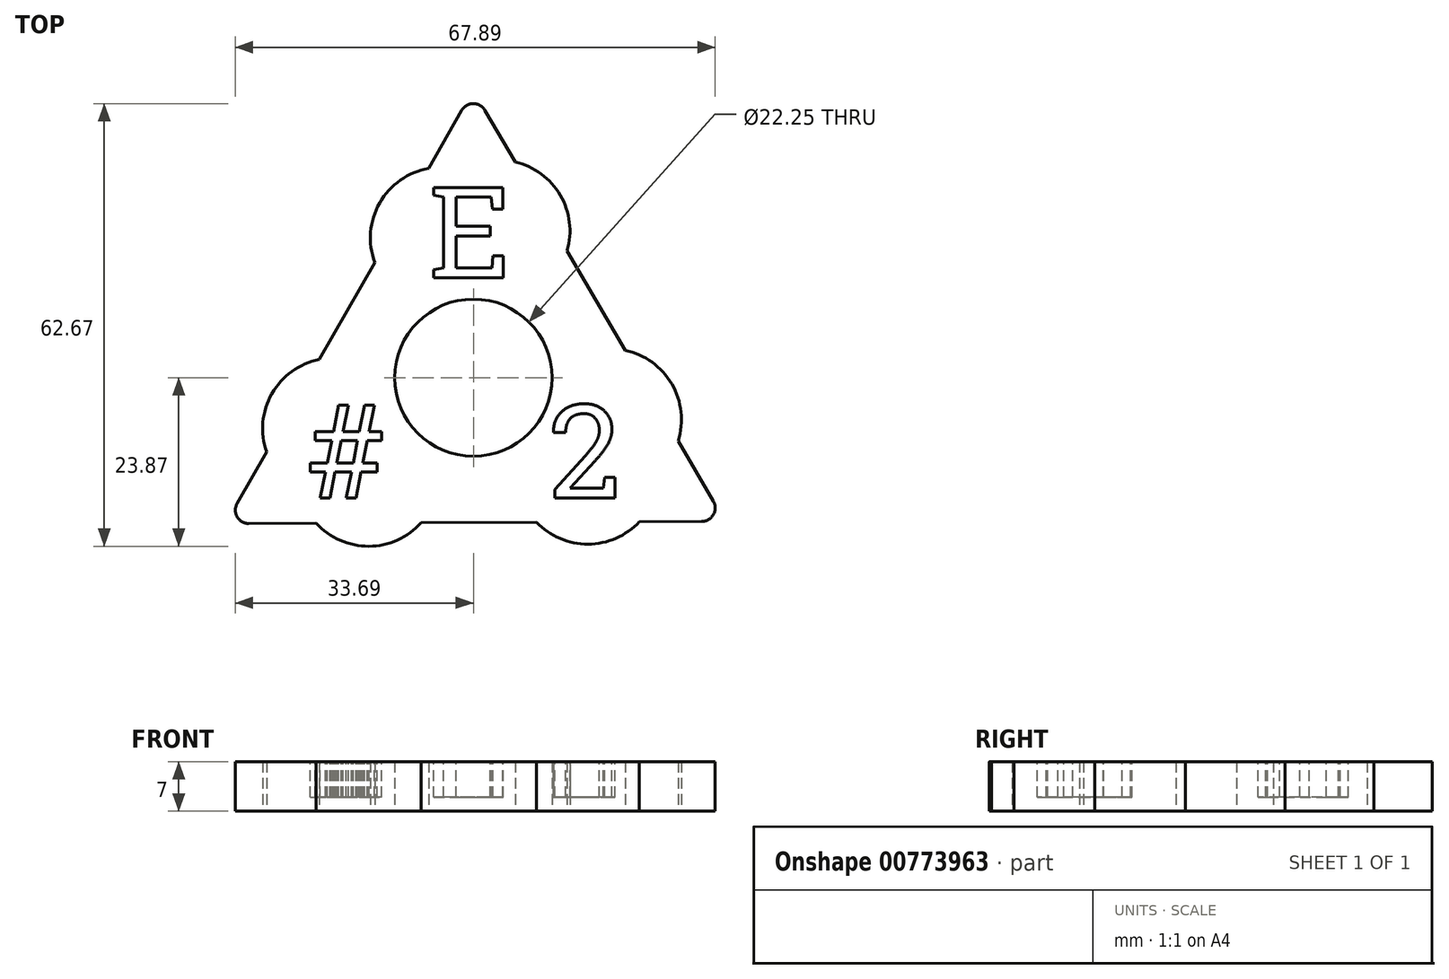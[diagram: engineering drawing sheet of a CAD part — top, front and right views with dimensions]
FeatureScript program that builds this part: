
annotation { "Feature Type Name" : "Feature", "Feature Type Description" : "" }
export const myFeature = defineFeature(function(context is Context, id is Id, definition is map)
    precondition{}
    {
        {
            var Q0;
            Q0=qCreatedBy(makeId("Top.planeOp"),FACE);
            var sketch = newSketch(context, id + "F0", { "sketchPlane" : qUnion([Q0])});
            skCircle(sketch, "E0", {"center": v(0, 0) * mm, "radius": 11.12 * mm});
            skLineSegment(sketch, "E1.0", {"start": v(-35.07, -20.67) * mm, "end": v(-0.02, 40.7) * mm});
            skLineSegment(sketch, "E1.1", {"start": v(-0.02, 40.7) * mm, "end": v(35.6, -20.33) * mm});
            skLineSegment(sketch, "E1.2", {"start": v(35.6, -20.33) * mm, "end": v(-35.07, -20.67) * mm});
            skPoint(sketch, "E1.0.midPoint", {"position": v(-17.55, 10.02) * mm});
            skArc(sketch, "E2", {"start": v(-6.34, 29.64) * mm, "mid": v(-13.27, 24.75) * mm, "end": v(-13.96, 16.3) * mm});
            skArc(sketch, "E3", {"start": v(-21.8, 2.58) * mm, "mid": v(-28.52, -2.27) * mm, "end": v(-29.27, -10.52) * mm});
            skArc(sketch, "E4.1.0", {"start": v(-22.5, -20.31) * mm, "mid": v(-14.8, -23.87) * mm, "end": v(-7.14, -20.24) * mm});
            skArc(sketch, "E4.1.1", {"start": v(8.67, -20.16) * mm, "mid": v(16.22, -23.56) * mm, "end": v(23.75, -20.1) * mm});
            skArc(sketch, "E4.2.0", {"start": v(28.84, -9.32) * mm, "mid": v(28.07, -0.89) * mm, "end": v(21.1, 3.93) * mm});
            skArc(sketch, "E4.2.1", {"start": v(13.13, 17.59) * mm, "mid": v(12.3, 25.83) * mm, "end": v(5.53, 30.61) * mm});
            skSolve(sketch);
        }
        {
            var Q0;
            Q0=qSketchRegion(id+"F0",true);
            extrude(context, id + "F1", {"entities" : qUnion([Q0]), "depth" : 7 * mm, "offsetDistance" : 25 * mm});
        }
        {
            var Q0;
            Q0=makeQuery(id+"F1.opExtrude","CAP_FACE",FACE,{"disambiguationData":[OSD([sQuery(id+"F0.wireOp",EDGE,"E0"),sQuery(id+"F0.wireOp",EDGE,"E1.0"),sQuery(id+"F0.wireOp",EDGE,"E1.1"),sQuery(id+"F0.wireOp",EDGE,"E1.2")])],"isStart":false});
            var sketch = newSketch(context, id + "F2", { "sketchPlane" : qUnion([Q0])});
            skText(sketch, "E5", { "text": "E\n", "fontName": "RobotoSlab-Regular.ttf"});
            skText(sketch, "E6", { "text": "#     2\n", "fontName": "RobotoSlab-Regular.ttf"});
            const initialGuessF2  = {"E5": [-0.00625, 0.01418, 1, 0, 0.0129], "E6": [-0.02363, -0.01704, 1, 0, 0.01333]};
            skSetInitialGuess(sketch, initialGuessF2);
            skSolve(sketch);
        }
        {
            var Q0;
            Q0=qSketchRegion(id+"F2",true);
            extrude(context, id + "F3", {"entities" : qUnion([Q0]), "operationType" : NewBodyOperationType.REMOVE, "oppositeDirection" : true, "depth" : 5 * mm, "offsetDistance" : 25 * mm});
        }
        {
            var Q0;
            Q0=makeQuery(id+"F1.opExtrude","SWEPT_EDGE",EDGE,{"disambiguationData":[OSD([sQuery(id+"F0.wireOp",EDGE,"E1.0"),sQuery(id+"F0.wireOp",EDGE,"E1.2")])]});
            var Q1;
            Q1=makeQuery(id+"F1.opExtrude","SWEPT_EDGE",EDGE,{"disambiguationData":[OSD([sQuery(id+"F0.wireOp",EDGE,"E1.0"),sQuery(id+"F0.wireOp",EDGE,"E1.1")])]});
            var Q2;
            Q2=makeQuery(id+"F1.opExtrude","SWEPT_EDGE",EDGE,{"disambiguationData":[OSD([sQuery(id+"F0.wireOp",EDGE,"E1.1"),sQuery(id+"F0.wireOp",EDGE,"E1.2")])]});
            fillet(context, id + "F4", {"entities" : qUnion([Q0, Q1, Q2]), "radius" : 1.9 * mm, "tangentPropagation" : true, "allowEdgeOverflow" : false});
        }
    });
